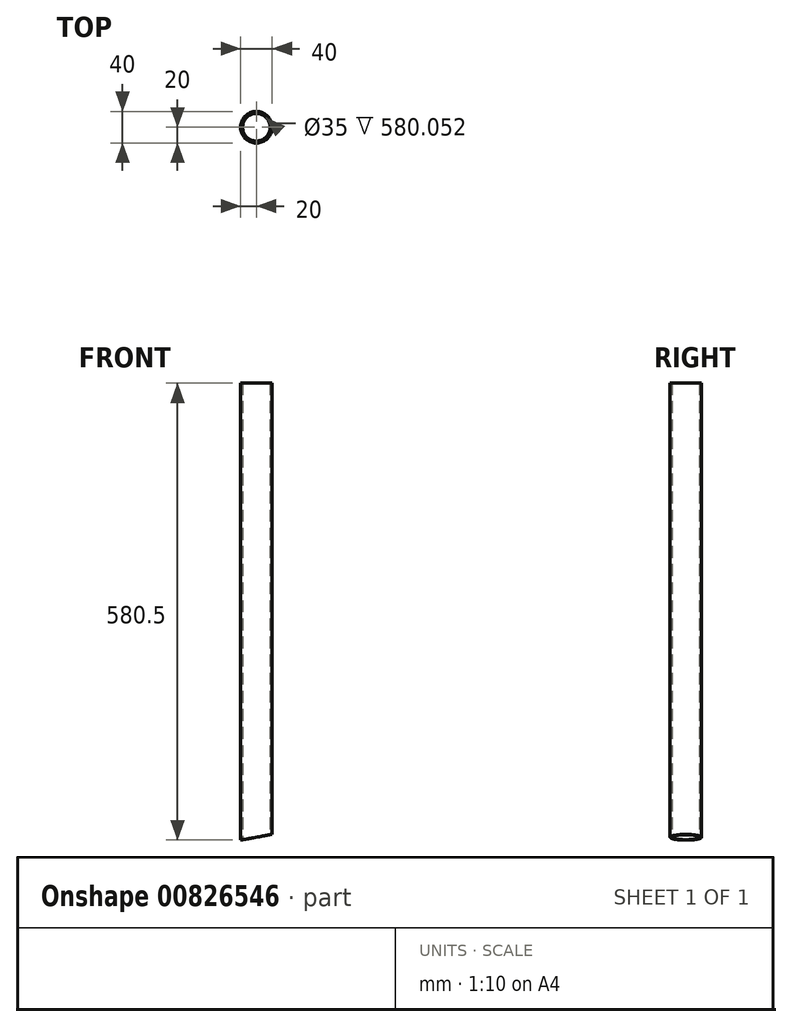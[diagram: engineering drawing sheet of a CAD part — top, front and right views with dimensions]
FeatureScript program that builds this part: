
annotation { "Feature Type Name" : "Feature", "Feature Type Description" : "" }
export const myFeature = defineFeature(function(context is Context, id is Id, definition is map)
    precondition{}
    {
        {
            var Q0;
            Q0=qCreatedBy(makeId("Top.planeOp"),FACE);
            var sketch = newSketch(context, id + "F0", { "sketchPlane" : qUnion([Q0])});
            skCircle(sketch, "E0", {"center": v(0, 0) * mm, "radius": 20 * mm});
            skCircle(sketch, "E1", {"center": v(0, 0) * mm, "radius": 17.5 * mm});
            skSolve(sketch);
        }
        {
            var Q0;
            Q0=makeQuery(id+"F0.imprint","IMPRINT",FACE,{"disambiguationData":[TD([[makeQuery(id+"F0.imprint","IMPRINT",EDGE,{"derivedFrom":sQuery(id+"F0.wireOp",EDGE,"E0")}),1.0]])]});
            extrude(context, id + "F1", {"entities" : qUnion([Q0]), "depth" : 580.5 * mm, "offsetDistance" : 25 * mm});
        }
        {
            var Q0;
            Q0=qCreatedBy(makeId("Front.planeOp"),FACE);
            var sketch = newSketch(context, id + "F2", { "sketchPlane" : qUnion([Q0])});
            skLineSegment(sketch, "E2", {"start": v(-20, 0) * mm, "end": v(0, 0) * mm});
            skLineSegment(sketch, "E3", {"start": v(0, 0) * mm, "end": v(20, 0) * mm});
            skLineSegment(sketch, "E4", {"start": v(20, 0) * mm, "end": v(20, 19.08) * mm});
            skLineSegment(sketch, "E5", {"start": v(-20, 0) * mm, "end": v(20, 7.2) * mm});
            skSolve(sketch);
        }
        {
            var Q0;
            Q0=qSketchRegion(id+"F2",true);
            extrude(context, id + "F3", {"entities" : qUnion([Q0]), "operationType" : NewBodyOperationType.REMOVE, "endBound" : BoundingType.SYMMETRIC, "oppositeDirection" : true, "depth" : 50 * mm, "offsetDistance" : 25 * mm});
        }
    });
